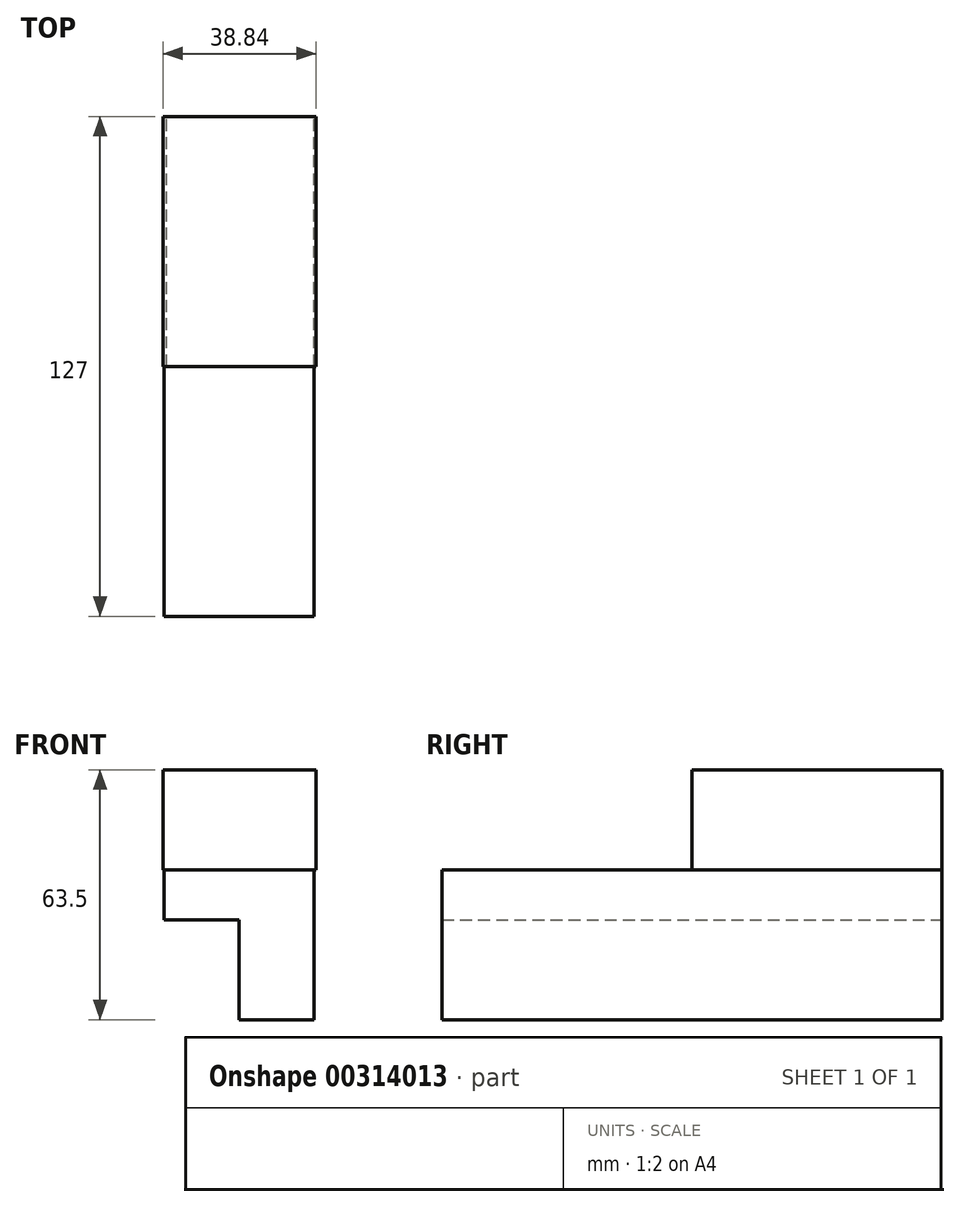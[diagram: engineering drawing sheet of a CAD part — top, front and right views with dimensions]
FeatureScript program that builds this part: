
annotation { "Feature Type Name" : "Feature", "Feature Type Description" : "" }
export const myFeature = defineFeature(function(context is Context, id is Id, definition is map)
    precondition{}
    {
        {
            var Q0;
            Q0=qCreatedBy(makeId("Front.planeOp"),FACE);
            var sketch = newSketch(context, id + "F0", { "sketchPlane" : qUnion([Q0])});
            skLineSegment(sketch, "E0", {"start": v(-17.1, 35.25) * mm, "end": v(-17.1, -28.25) * mm});
            skLineSegment(sketch, "E1", {"start": v(-17.1, -28.25) * mm, "end": v(-36.9, -28.25) * mm});
            skLineSegment(sketch, "E2", {"start": v(-36.9, -28.25) * mm, "end": v(-36.9, -2.85) * mm});
            skLineSegment(sketch, "E3", {"start": v(-36.9, -2.85) * mm, "end": v(-55.95, -2.85) * mm});
            skLineSegment(sketch, "E4", {"start": v(-55.95, -2.85) * mm, "end": v(-55.95, 9.85) * mm});
            skLineSegment(sketch, "E5", {"start": v(-55.95, 9.85) * mm, "end": v(-55.95, 35.25) * mm});
            skLineSegment(sketch, "E6", {"start": v(-55.95, 35.25) * mm, "end": v(-17.1, 35.25) * mm});
            skLineSegment(sketch, "E7", {"start": v(-55.95, 9.85) * mm, "end": v(-17.1, 9.85) * mm});
            skSolve(sketch);
        }
        {
            var Q0;
            Q0=makeQuery(id+"F0.imprint","IMPRINT",FACE,{"disambiguationData":[TD([[makeQuery(id+"F0.imprint","IMPRINT",EDGE,{"derivedFrom":sQuery(id+"F0.wireOp",EDGE,"E5")}),-1.0]])]});
            extrude(context, id + "F1", {"entities" : qUnion([Q0]), "depth" : 63.5 * mm});
        }
        {
            var Q0;
            Q0=qCreatedBy(makeId("Front.planeOp"),FACE);
            var sketch = newSketch(context, id + "F2", { "sketchPlane" : qUnion([Q0])});
            skLineSegment(sketch, "E8", {"start": v(-55.67, 9.85) * mm, "end": v(-55.67, -2.85) * mm});
            skLineSegment(sketch, "E9", {"start": v(-55.67, -2.85) * mm, "end": v(-36.62, -2.85) * mm});
            skLineSegment(sketch, "E10", {"start": v(-36.62, -2.85) * mm, "end": v(-36.62, -28.25) * mm});
            skLineSegment(sketch, "E11", {"start": v(-36.62, -28.25) * mm, "end": v(-17.57, -28.25) * mm});
            skLineSegment(sketch, "E12", {"start": v(-17.57, -28.25) * mm, "end": v(-17.57, 9.76) * mm});
            skLineSegment(sketch, "E13", {"start": v(-55.67, 9.85) * mm, "end": v(-17.57, 9.76) * mm});
            skSolve(sketch);
        }
        {
            var Q0;
            Q0 = qSketchRegion(id + "F2", true);
            extrude(context, id + "F3", {"entities" : qUnion([Q0]), "operationType" : NewBodyOperationType.ADD, "depth" : 127 * mm});
        }
    });
